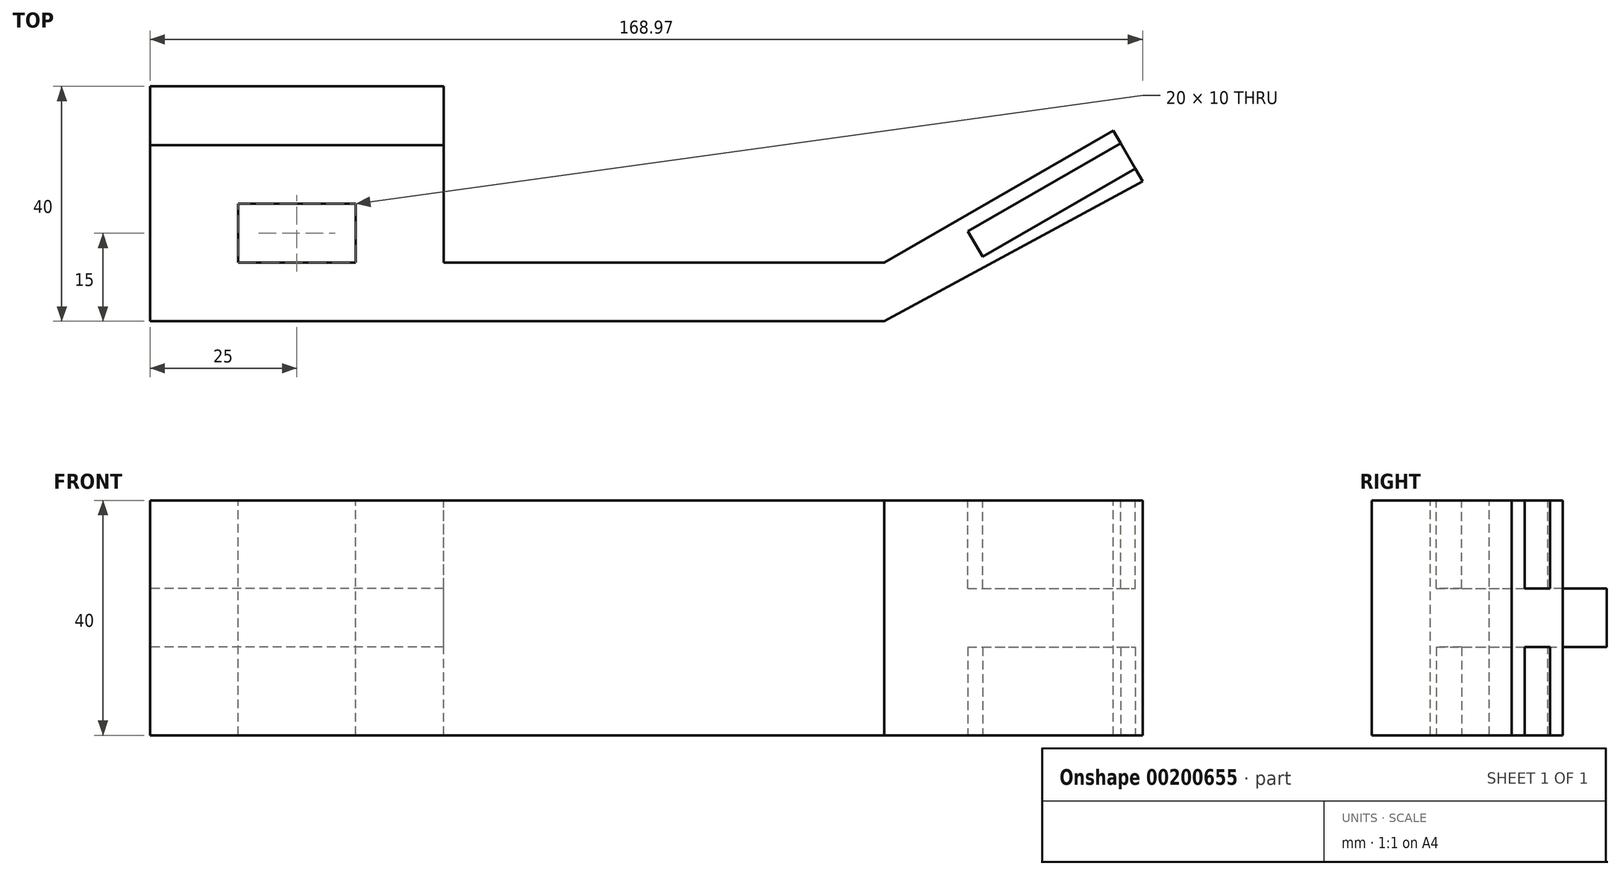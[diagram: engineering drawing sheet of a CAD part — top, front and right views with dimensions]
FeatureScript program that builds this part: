
annotation { "Feature Type Name" : "Feature", "Feature Type Description" : "" }
export const myFeature = defineFeature(function(context is Context, id is Id, definition is map)
    precondition{}
    {
        {
            var Q0;
            Q0=qCreatedBy(makeId("Front.planeOp"),FACE);
            var sketch = newSketch(context, id + "F0", { "sketchPlane" : qUnion([Q0])});
            skLineSegment(sketch, "E0.bottom", {"start": v(62.5, -20) * mm, "end": v(-62.5, -20) * mm});
            skLineSegment(sketch, "E0.top", {"start": v(62.5, 20) * mm, "end": v(-62.5, 20) * mm});
            skLineSegment(sketch, "E0.left", {"start": v(62.5, -20) * mm, "end": v(62.5, 20) * mm});
            skLineSegment(sketch, "E0.right", {"start": v(-62.5, -20) * mm, "end": v(-62.5, 20) * mm});
            skPoint(sketch, "E0.middle", {"position": v(0, 0) * mm});
            skSolve(sketch);
        }
        {
            var Q0;
            Q0=makeQuery(id+"F0.imprint","IMPRINT",FACE,{"disambiguationData":[TD([[makeQuery(id+"F0.imprint","IMPRINT",EDGE,{"derivedFrom":sQuery(id+"F0.wireOp",EDGE,"E0.bottom")}),-1.0]])]});
            extrude(context, id + "F1", {"entities" : qUnion([Q0]), "depth" : 10 * mm});
        }
        {
            var Q0;
            Q0=makeQuery(id+"F1.opExtrude","SWEPT_FACE",FACE,{"disambiguationData":[OSD([sQuery(id+"F0.wireOp",EDGE,"E0.right")])]});
            var sketch = newSketch(context, id + "F2", { "sketchPlane" : qUnion([Q0])});
            skLineSegment(sketch, "E1", {"start": v(0, -20) * mm, "end": v(-20, -20) * mm});
            skLineSegment(sketch, "E2", {"start": v(-20, -20) * mm, "end": v(-20, -5) * mm});
            skLineSegment(sketch, "E3", {"start": v(-20, -5) * mm, "end": v(-30, -5) * mm});
            skLineSegment(sketch, "E4", {"start": v(-30, -5) * mm, "end": v(-30, 5) * mm});
            skLineSegment(sketch, "E5", {"start": v(-30, 5) * mm, "end": v(-20, 5) * mm});
            skLineSegment(sketch, "E6", {"start": v(-20, 5) * mm, "end": v(-20, 20) * mm});
            skLineSegment(sketch, "E7", {"start": v(-20, 20) * mm, "end": v(0, 20) * mm});
            skLineSegment(sketch, "E8", {"start": v(0, 0) * mm, "end": v(-30, 0) * mm});
            skSolve(sketch);
        }
        {
            var Q0;
            {var subQ3=sQuery(id+"F2.wireOp",EDGE,"E1");Q0=makeQuery(id+"F2.imprint","IMPRINT",FACE,{"disambiguationData":[TD([[makeQuery(id+"F2.imprint","IMPRINT",EDGE,{"derivedFrom":subQ3}),-1.0]])]});}
            var Q1;
            {var subQ4=sQuery(id+"F2.wireOp",EDGE,"E5");Q1=makeQuery(id+"F2.imprint","IMPRINT",FACE,{"disambiguationData":[TD([[makeQuery(id+"F2.imprint","IMPRINT",EDGE,{"derivedFrom":subQ4}),-1.0]])]});}
            extrude(context, id + "F3", {"entities" : qUnion([Q0, Q1]), "operationType" : NewBodyOperationType.ADD, "oppositeDirection" : true, "depth" : 50 * mm});
        }
        {
            var Q0;
            Q0=makeQuery(id+"F3.boolean.opBoolean","MERGE",FACE,{"derivedFrom":[makeQuery(id+"F1.opExtrude","SWEPT_FACE",FACE,{"disambiguationData":[OSD([sQuery(id+"F0.wireOp",EDGE,"E0.top")])]}),makeQuery(id+"F3.opExtrude","SWEPT_FACE",FACE,{"disambiguationData":[OSD([sQuery(id+"F2.wireOp",EDGE,"E7")])]})]});
            var sketch = newSketch(context, id + "F4", { "sketchPlane" : qUnion([Q0])});
            skLineSegment(sketch, "E9", {"start": v(-27.5, 0) * mm, "end": v(-47.5, 0) * mm});
            skLineSegment(sketch, "E10.bottom", {"start": v(-47.5, 10) * mm, "end": v(-27.5, 10) * mm});
            skLineSegment(sketch, "E10.top", {"start": v(-47.5, 0) * mm, "end": v(-27.5, 0) * mm});
            skLineSegment(sketch, "E10.left", {"start": v(-47.5, 10) * mm, "end": v(-47.5, 0) * mm});
            skLineSegment(sketch, "E10.right", {"start": v(-27.5, 10) * mm, "end": v(-27.5, 0) * mm});
            skSolve(sketch);
        }
        {
            var Q0;
            Q0=makeQuery(id+"F4.imprint","IMPRINT",FACE,{"disambiguationData":[TD([[makeQuery(id+"F4.imprint","IMPRINT",EDGE,{"derivedFrom":sQuery(id+"F4.wireOp",EDGE,"E10.bottom")}),-1.0]])]});
            extrude(context, id + "F5", {"entities" : qUnion([Q0]), "operationType" : NewBodyOperationType.REMOVE, "endBound" : BoundingType.UP_TO_NEXT, "oppositeDirection" : true, "depth" : 25 * mm, "hasSecondDirection" : true, "secondDirectionOppositeDirection" : false, "secondDirectionDepth" : 25 * mm});
        }
        {
            var Q0;
            Q0=makeQuery(id+"F3.boolean.opBoolean","MERGE",FACE,{"derivedFrom":[makeQuery(id+"F1.opExtrude","SWEPT_FACE",FACE,{"disambiguationData":[OSD([sQuery(id+"F0.wireOp",EDGE,"E0.top")])]}),makeQuery(id+"F3.opExtrude","SWEPT_FACE",FACE,{"disambiguationData":[OSD([sQuery(id+"F2.wireOp",EDGE,"E7")])]})]});
            var sketch = newSketch(context, id + "F6", { "sketchPlane" : qUnion([Q0])});
            skLineSegment(sketch, "E11", {"start": v(62.5, 0) * mm, "end": v(101.47, 22.5) * mm});
            skLineSegment(sketch, "E12", {"start": v(101.47, 22.5) * mm, "end": v(106.47, 13.84) * mm});
            skLineSegment(sketch, "E13", {"start": v(106.47, 13.84) * mm, "end": v(62.5, -10) * mm});
            skLineSegment(sketch, "E14", {"start": v(62.5, -10) * mm, "end": v(62.5, 0) * mm});
            skSolve(sketch);
        }
        {
            var Q0;
            Q0=makeQuery(id+"F6.imprint","IMPRINT",FACE,{"disambiguationData":[TD([[makeQuery(id+"F6.imprint","IMPRINT",EDGE,{"derivedFrom":sQuery(id+"F6.wireOp",EDGE,"E11")}),-1.0]])]});
            extrude(context, id + "F7", {"entities" : qUnion([Q0]), "operationType" : NewBodyOperationType.ADD, "oppositeDirection" : true, "depth" : 40 * mm});
        }
        {
            var Q0;
            Q0=makeQuery(id+"F7.opExtrude","SWEPT_FACE",FACE,{"disambiguationData":[OSD([sQuery(id+"F6.wireOp",EDGE,"E12")])]});
            var sketch = newSketch(context, id + "F8", { "sketchPlane" : qUnion([Q0])});
            skLineSegment(sketch, "E15", {"start": v(-41.25, 0) * mm, "end": v(-38.75, 0) * mm});
            skLineSegment(sketch, "E16", {"start": v(-33.75, 0) * mm, "end": v(-33.75, 20) * mm});
            skLineSegment(sketch, "E17", {"start": v(-33.75, 0) * mm, "end": v(-33.75, -20) * mm});
            skLineSegment(sketch, "E18", {"start": v(-38.75, 0) * mm, "end": v(-38.75, 20) * mm});
            skLineSegment(sketch, "E19", {"start": v(-38.75, 0) * mm, "end": v(-38.75, -20) * mm});
            skLineSegment(sketch, "E20", {"start": v(-33.75, 5) * mm, "end": v(-38.75, 5) * mm});
            skLineSegment(sketch, "E21", {"start": v(-33.75, -5) * mm, "end": v(-38.75, -5) * mm});
            skLineSegment(sketch, "E22.trimOffspring", {"start": v(-33.75, 0) * mm, "end": v(-31.25, 0) * mm});
            skSolve(sketch);
        }
        {
            var Q0;
            {var subQ3=sQuery(id+"F8.wireOp",EDGE,"E21");Q0=makeQuery(id+"F8.imprint","IMPRINT",FACE,{"disambiguationData":[TD([[makeQuery(id+"F8.imprint","IMPRINT",EDGE,{"derivedFrom":subQ3}),1.0]])]});}
            var Q1;
            {var subQ3=sQuery(id+"F8.wireOp",EDGE,"E20");Q1=makeQuery(id+"F8.imprint","IMPRINT",FACE,{"disambiguationData":[TD([[makeQuery(id+"F8.imprint","IMPRINT",EDGE,{"derivedFrom":subQ3}),-1.0]])]});}
            extrude(context, id + "F9", {"entities" : qUnion([Q0, Q1]), "operationType" : NewBodyOperationType.REMOVE, "oppositeDirection" : true, "depth" : 30 * mm});
        }
    });
